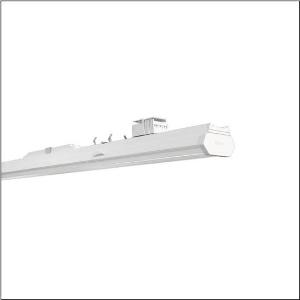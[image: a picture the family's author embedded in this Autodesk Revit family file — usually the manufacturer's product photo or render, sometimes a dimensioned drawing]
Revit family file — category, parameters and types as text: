
# Revit family: licross_r__11_protected_mo_51tp11dn495g_6ace
name_source: partatom
category: Lighting Fixtures
units: mm (PartAtom-declared; Revit-internal decimal feet)

## family parameters
Cut with Voids When Loaded = No
Host = Face
Light Source = No
Part Type = Normal
Room Calculation Point = No
Round Connector Dimension = Use Diameter
Shared = No

## types (1)
- --- (1 x LED, 9930 lm, 57.1 W, 4000K)
    Apparent Load = 57 VA
    CIE Flux Codes = 83 94 98 100 100
    Color Rendering = 80
    Color Temperature = 4000K
    Default Elevation = 1800 mm
    Description = Licross® 11 Protected MO, luminaire insert, of sheet steel, galvanised, coil coated, white, length: 1.500mm, width: 90mm, height: 101mm, LED rated luminous flux: 9.980lm, light colour: 840, control gear: DALI 2, with plug, 5-pole, with phase selection, mains connection: 220..240V, AC, 50/60Hz, rated input power: 57W, halogen-free wiring, primary light control with lens, of plastic, primary optical cover: cover, of PMMA, light emission: direct distribution, primary light characteristic: symmetric, protection rating (complete): IP64, insulation class (complete): insulation class I (protective earthing), certification: CE, ENEC, VDE, UKCA, protection symbol: D if used in an environment with conductive dust loads with corresponding accessories, impact resistance: IK06, permissible ambient temperature for indoor applications: -25..+35°C, corresponds to IFS (International Featured Standards) requirements for safety and quality in the food industry, reducing of maximum allowable ambient temperature of 5°C with ceiling mounting, LABS conformity tested according to VDMA 24364:2018-05, packaging unit: 1 piece
    Height = 92 mm
    Lamp = 1 x LED
    Lamp Light Flux = 9930 lm
    Lamp Power = 57.1 W
    Lamp count = 1
    Length = 1500 mm
    Luminous efficacy = 174 lm/W
    Manufacturer = Siteco
    ModVariant = No
    Model = 51TP11DN495G
    Mounting Place = Ceiling
    Mounting Type = Pendant
    Number of Poles = 1
    OnlyDefault = Yes
    Power Factor = 1
    Product Name = Licross® 11 Protected MO
    Product group = luminaire insert
    ProductGroupID = 901
    Protection Class = Protection class I
    Protection Degree = IP 64
    RLX_Detail_Level = 1
    RLX_Emergency_Light_Flux = 0 lm
    RLX_Emergency_Type = 0
    RLX_Emergency_Type_DB = No
    RlxData = <blob elided: 24133 chars, md5=9365007b>
    Socket = socket
    Standby Power = 0 W
    System Light Flux = 9930 lm
    System Power = 57 W
    Type Comments = factory setting: luminous flux: 100 % | dim-lin: 254 | 378 mA
    Type Image = l_1256148.jpg
    URL = http://relux.com
    VarID = @adj_069819
    Voltage = 0 V
    Weight = 0.00 kg
    Width = 88 mm

## geometry (parser evidence)
native form markers: Blend x4, Sweep x12
no freeform markers — native parametric forms only
